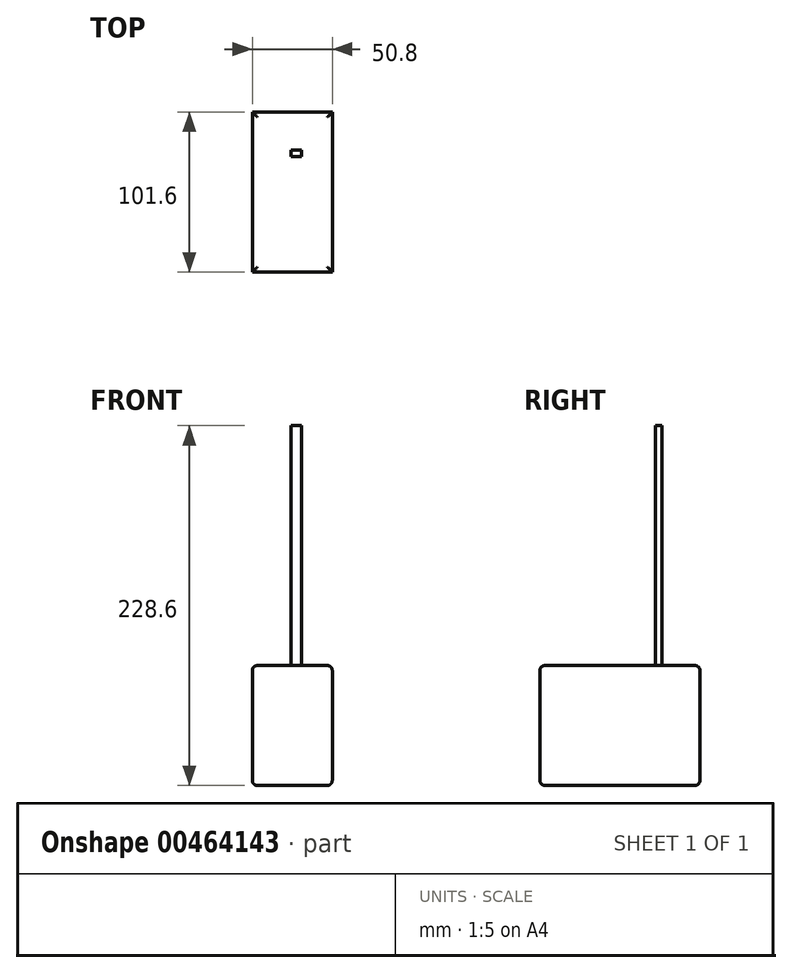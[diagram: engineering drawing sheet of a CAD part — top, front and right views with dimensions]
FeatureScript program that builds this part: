
annotation { "Feature Type Name" : "Feature", "Feature Type Description" : "" }
export const myFeature = defineFeature(function(context is Context, id is Id, definition is map)
    precondition{}
    {
        {
            var Q0;
            Q0=qCreatedBy(makeId("Front.planeOp"),FACE);
            var sketch = newSketch(context, id + "F0", { "sketchPlane" : qUnion([Q0])});
            skLineSegment(sketch, "E0", {"start": v(0, 0) * mm, "end": v(50.8, 0) * mm});
            skLineSegment(sketch, "E1", {"start": v(50.8, 0) * mm, "end": v(50.8, 76.2) * mm});
            skLineSegment(sketch, "E2", {"start": v(50.8, 76.2) * mm, "end": v(0, 76.2) * mm});
            skLineSegment(sketch, "E3", {"start": v(0, 76.2) * mm, "end": v(0, 0) * mm});
            skSolve(sketch);
        }
        {
            var Q0;
            Q0=makeQuery(id+"F0.imprint","IMPRINT",FACE,{"disambiguationData":[TD([[makeQuery(id+"F0.imprint","IMPRINT",EDGE,{"derivedFrom":sQuery(id+"F0.wireOp",EDGE,"E0")}),1.0]])]});
            extrude(context, id + "F1", {"entities" : qUnion([Q0]), "depth" : 101.6 * mm});
        }
        {
            var Q0;
            Q0=makeQuery(id+"F1.opExtrude","SWEPT_FACE",FACE,{"disambiguationData":[OSD([sQuery(id+"F0.wireOp",EDGE,"E2")])]});
            var Q1;
            Q1=makeQuery(id+"F1.opExtrude","SWEPT_FACE",FACE,{"disambiguationData":[OSD([sQuery(id+"F0.wireOp",EDGE,"E0")])]});
            fillet(context, id + "F2", {"entities" : qUnion([Q0, Q1]), "radius" : 3.17 * mm, "tangentPropagation" : true, "allowEdgeOverflow" : false});
        }
        {
            var Q0;
            Q0=makeQuery(id+"F1.opExtrude","SWEPT_FACE",FACE,{"disambiguationData":[OSD([sQuery(id+"F0.wireOp",EDGE,"E2")])]});
            var sketch = newSketch(context, id + "F3", { "sketchPlane" : qUnion([Q0])});
            skLineSegment(sketch, "E4.bottom", {"start": v(19.04, -32.5) * mm, "end": v(32.8, -32.5) * mm});
            skLineSegment(sketch, "E4.top", {"start": v(19.04, -74.17) * mm, "end": v(32.8, -74.17) * mm});
            skLineSegment(sketch, "E4.left", {"start": v(19.04, -32.5) * mm, "end": v(19.04, -74.17) * mm});
            skLineSegment(sketch, "E4.right", {"start": v(32.8, -32.5) * mm, "end": v(32.8, -74.17) * mm});
            skLineSegment(sketch, "E5.bottom", {"start": v(24.62, -28.23) * mm, "end": v(31.4, -28.23) * mm});
            skLineSegment(sketch, "E5.top", {"start": v(24.62, -24.12) * mm, "end": v(31.4, -24.12) * mm});
            skLineSegment(sketch, "E5.left", {"start": v(24.62, -28.23) * mm, "end": v(24.62, -24.12) * mm});
            skLineSegment(sketch, "E5.right", {"start": v(31.4, -28.23) * mm, "end": v(31.4, -24.12) * mm});
            skSolve(sketch);
        }
        {
            var Q0;
            Q0=makeQuery(id+"F3.imprint","IMPRINT",FACE,{"disambiguationData":[TD([[makeQuery(id+"F3.imprint","IMPRINT",EDGE,{"derivedFrom":sQuery(id+"F3.wireOp",EDGE,"E5.bottom")}),1.0]])]});
            extrude(context, id + "F4", {"entities" : qUnion([Q0]), "operationType" : NewBodyOperationType.ADD, "depth" : 152.4 * mm, "offsetDistance" : 25.4 * mm});
        }
    });
